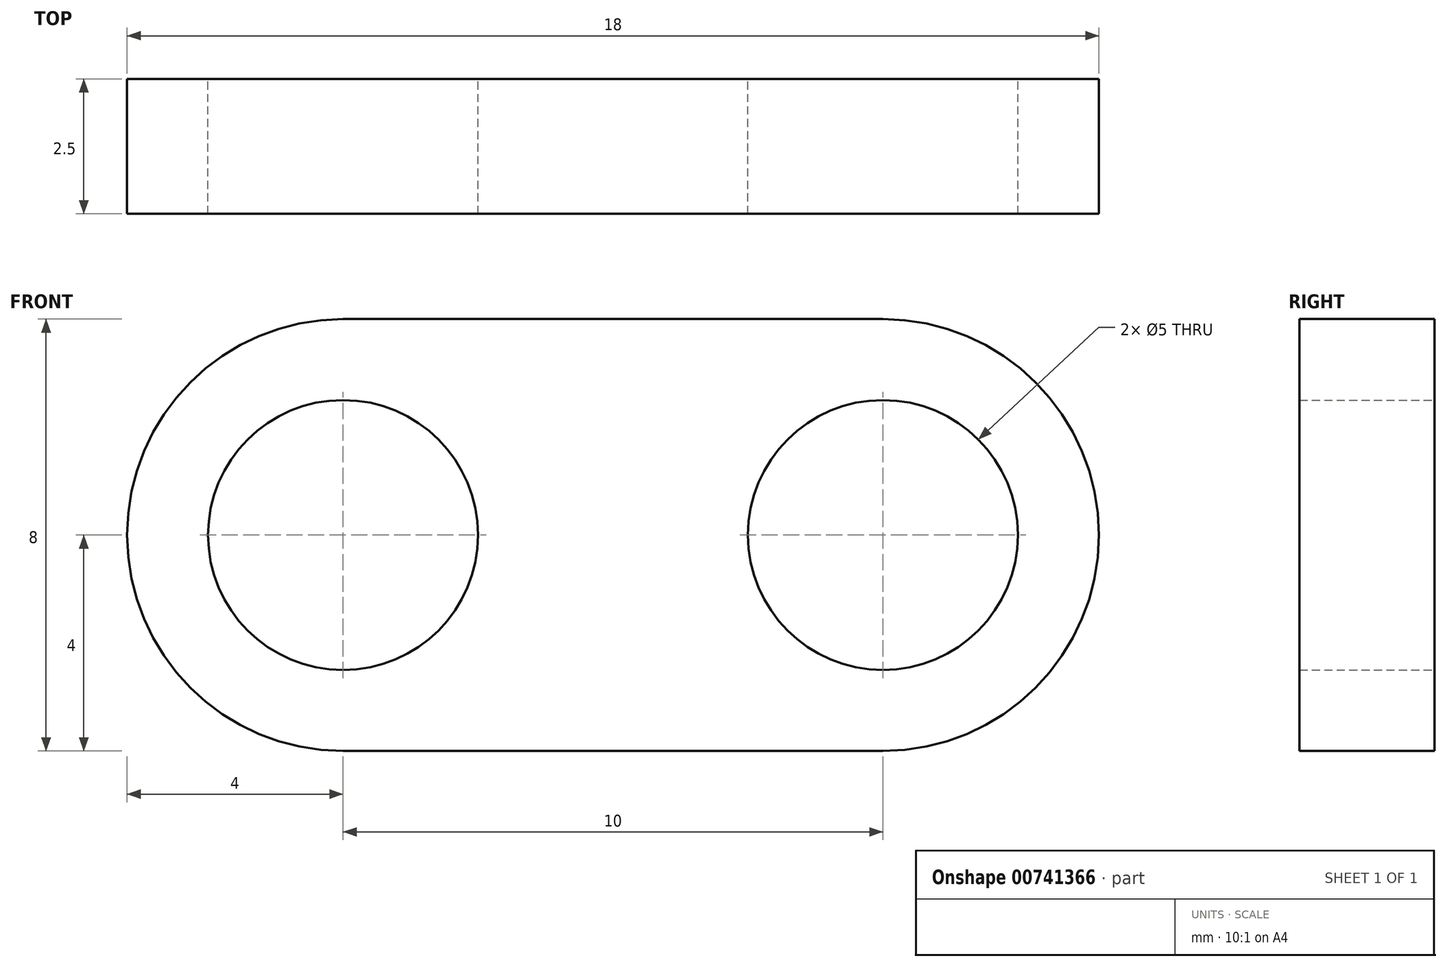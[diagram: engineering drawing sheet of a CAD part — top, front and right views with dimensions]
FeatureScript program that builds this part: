
annotation { "Feature Type Name" : "Feature", "Feature Type Description" : "" }
export const myFeature = defineFeature(function(context is Context, id is Id, definition is map)
    precondition{}
    {
        {
            var Q0;
            Q0=qCreatedBy(makeId("Front.planeOp"),FACE);
            var sketch = newSketch(context, id + "F0", { "sketchPlane" : qUnion([Q0])});
            skArc(sketch, "E0", {"start": v(0, 4) * mm, "mid": v(-4, 0) * mm, "end": v(0, -4) * mm});
            skCircle(sketch, "E1", {"center": v(0, 0) * mm, "radius": 2.5 * mm});
            skLineSegment(sketch, "E2", {"start": v(0, 0) * mm, "end": v(10, 0) * mm, "construction": true});
            skArc(sketch, "E3", {"start": v(10, -4) * mm, "mid": v(14, 0) * mm, "end": v(10, 4) * mm});
            skCircle(sketch, "E4", {"center": v(10, 0) * mm, "radius": 2.5 * mm});
            skLineSegment(sketch, "E5.0", {"start": v(0, -4) * mm, "end": v(10, -4) * mm});
            skLineSegment(sketch, "E6.0", {"start": v(0, 4) * mm, "end": v(10, 4) * mm});
            skSolve(sketch);
        }
        {
            var Q0;
            Q0 = qSketchRegion(id + "F0", true);
            extrude(context, id + "F1", {"entities" : qUnion([Q0]), "depth" : 2.5 * mm, "offsetDistance" : 25 * mm});
        }
    });
